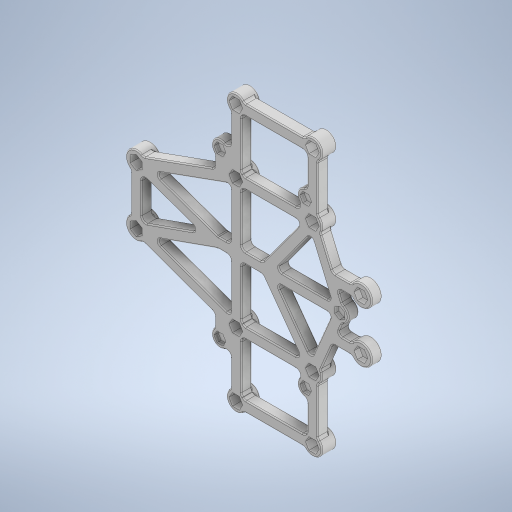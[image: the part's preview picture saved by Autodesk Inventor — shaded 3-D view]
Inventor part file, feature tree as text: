
AUTODESK INVENTOR PART (.ipt)
format: ipt  version: 2024.2 (Build 282272000, 272)  size: 1,460,224 bytes
history: native  units: mm
features: sketch x11, extrude x9, reference x8, fillet x3, other x3, hole x2
ambient origin geometry x8: Origin, YZ Plane, XZ Plane, XY Plane, X Axis, Y Axis, Z Axis, Center Point
bodies: Solid1 (feature_tree)
feature tree (36):
  extrude  "Extrusion1"  Depth=8.0mm
  extrude  "Extrusion2"  Depth=72.4mm
  extrude  "Extrusion5"  Depth=42.0mm
  extrude  "Extrusion3"  Depth=10.0mm
  extrude  "Extrusion4"  Depth=16.0mm
  extrude  "Extrusion6"  Depth=5.0mm
  hole  "Hole1"  [1 undecoded]
  hole  "Hole2"  [1 undecoded]
  fillet  "Fillet1"  Radius=5.0mm
  fillet  "Fillet2"  Radius=2.5mm
  fillet  "Fillet4"  Radius=2.5mm
  extrude  "Extrusion7"  Depth=5.0mm
  extrude  "Extrusion8"  Depth=5.0mm
  extrude  "Extrusion9"  Depth=2.0mm
  sketch  "Sketch2"  dims[d1=65.0mm d2=8.0mm]
  reference  "Reference10"
  reference  "Reference11"
  reference  "Reference12"
  reference  "Reference13"
  reference  "Reference14"
  reference  "Reference15"
  reference  "Reference16"
  reference  "Reference17"
  sketch  "Sketch3"  dims[d3=4.8mm d4=72.4mm]
  sketch  "Sketch4"  dims[d5=96.0mm d8=42.0mm]
  sketch  "Sketch5"  dims[d9=10.0mm d10=27.0mm]
  sketch  "Sketch6"  dims[d11=5.0mm d13=16.0mm]
  sketch  "Sketch7"  dims[d14=65.0mm d15=5.0mm]
  sketch  "Sketch8"  dims[d16=5.0mm d17=5.0mm]
  sketch  "Sketch9"  dims[d18=2.5mm d19=2.5mm d21=5.0mm d22=2.5mm d23=2.5mm]
  sketch  "Sketch10"  dims[d24=2.5mm d27=5.0mm]
  sketch  "Sketch11"  dims[d28=5.0mm d29=5.0mm]
  sketch  "Sketch12"  dims[d30=5.0mm d31=5.0mm d32=2.5mm d33=2.5mm d34=5.0mm d35=2.5mm d36=10.0mm d37=5.0mm d38=5.0mm d39=2.5mm d40=2.5mm d41=6.0mm d42=5.0mm d43=0.0mm d44=5.6mm d45=5.6mm d46=2.5mm d47=2.5mm d48=10.0mm d49=5.0mm d50=2.5mm d51=10.0mm d52=12.0mm d53=5.6mm d54=4.5mm d55=0.0mm d56=1.9mm d57=0.0mm d58=4.5mm d59=0.0mm d60=3.5mm d61=6.0mm d62=4.0mm d63=2.0mm d64=90.0deg d65=1.0mm d66=0.0mm d67=2.0mm d68=1.5mm d70=5.25mm d71=6.0mm d72=4.0mm d73=2.0mm d74=90.0deg d75=1.6mm d76=0.0mm d77=2.5mm d78=0.0mm d79=2.0mm d80=0.0mm d81=0.5mm d82=0.2mm d83=0.0mm d84=0.2mm d85=0.0mm d86=0.2mm d87=0.0mm]
  other  "<userpath>\Desktop\scioly-robot-tour\Hardware\ipt\v4\v4assembly.iam"
  other  "v4assembly.iam"
  other  "v4motormount:1"
note: 2 required parameter values undecoded (feature->parameter linkage not recoverable at this tier; creation-order binding heuristic only, values carry confidence <= 0.55)
